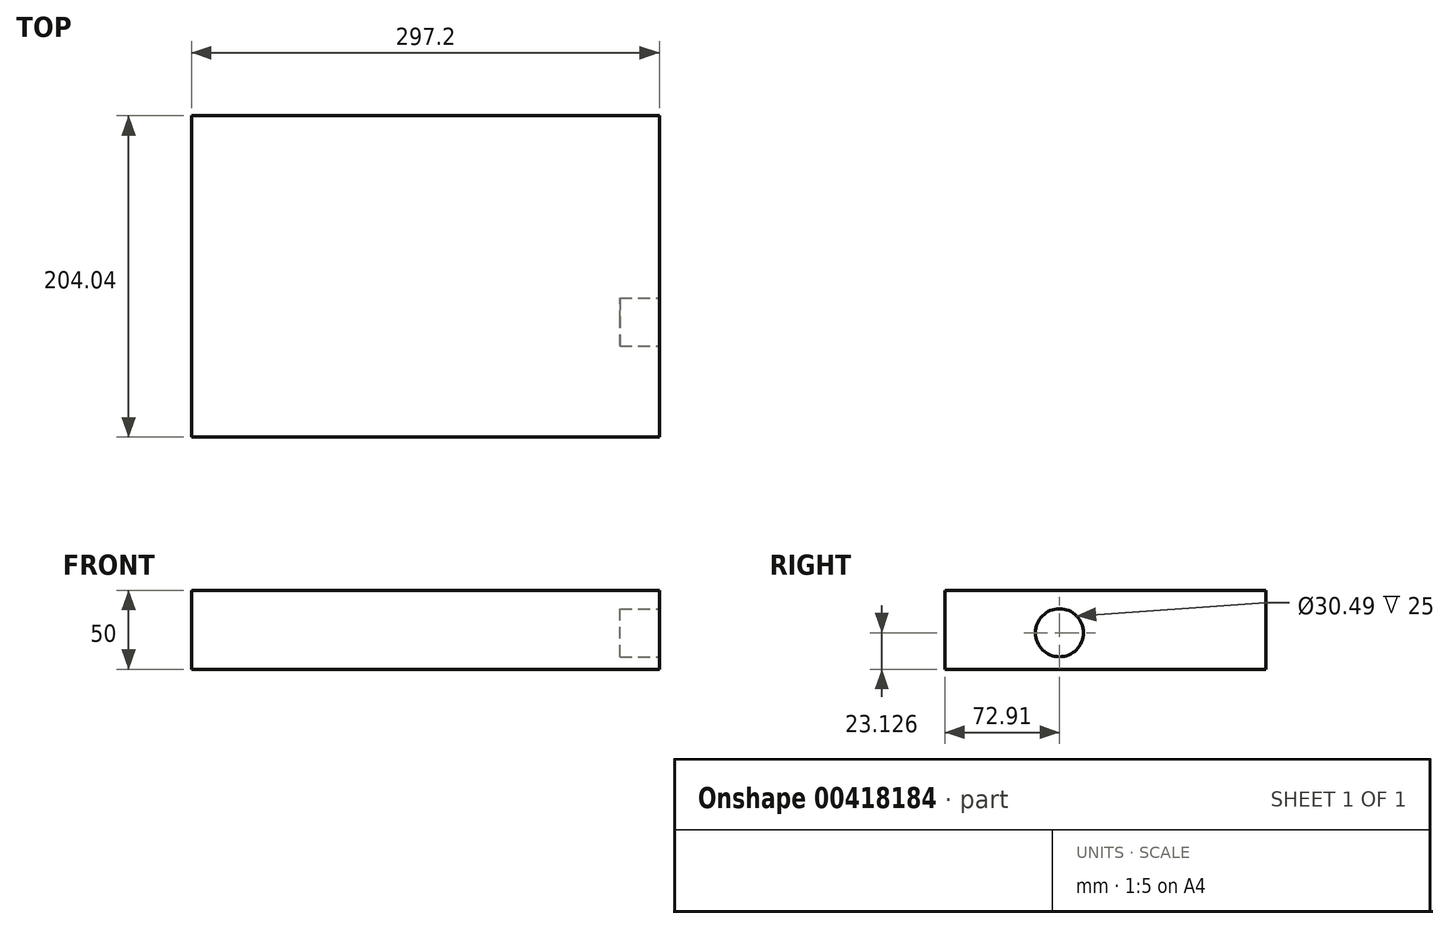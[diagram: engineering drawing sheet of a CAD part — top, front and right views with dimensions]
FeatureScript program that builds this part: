
annotation { "Feature Type Name" : "Feature", "Feature Type Description" : "" }
export const myFeature = defineFeature(function(context is Context, id is Id, definition is map)
    precondition{}
    {
        {
            var Q0;
            Q0=qCreatedBy(makeId("Top.planeOp"),FACE);
            var sketch = newSketch(context, id + "F0", { "sketchPlane" : qUnion([Q0])});
            skLineSegment(sketch, "E0.bottom", {"start": v(89.3, -89.62) * mm, "end": v(-207.89, -89.62) * mm});
            skLineSegment(sketch, "E0.top", {"start": v(89.3, 114.42) * mm, "end": v(-207.89, 114.42) * mm});
            skLineSegment(sketch, "E0.left", {"start": v(89.3, -89.62) * mm, "end": v(89.3, 114.42) * mm});
            skLineSegment(sketch, "E0.right", {"start": v(-207.89, -89.62) * mm, "end": v(-207.89, 114.42) * mm});
            skPoint(sketch, "E0.middle", {"position": v(-59.3, 12.4) * mm});
            skSolve(sketch);
        }
        {
            var Q0;
            Q0 = qSketchRegion(id + "F0", true);
            extrude(context, id + "F1", {"entities" : qUnion([Q0]), "depth" : 50 * mm});
        }
        {
            var Q0;
            Q0=makeQuery(id+"F1.opExtrude","SWEPT_FACE",FACE,{"disambiguationData":[OSD([sQuery(id+"F0.wireOp",EDGE,"E0.left")])]});
            var sketch = newSketch(context, id + "F2", { "sketchPlane" : qUnion([Q0])});
            skCircle(sketch, "E1", {"center": v(-16.7, 23.13) * mm, "radius": 15.24 * mm});
            skSolve(sketch);
        }
        {
            var Q0;
            Q0=makeQuery(id+"F2.imprint","IMPRINT",FACE,{"disambiguationData":[TD([[makeQuery(id+"F2.imprint","IMPRINT",EDGE,{"derivedFrom":sQuery(id+"F2.wireOp",EDGE,"E1")}),1.0]])]});
            var Q1;
            Q1=sQuery(id+"F2.wireOp",EDGE,"E1");
            extrude(context, id + "F3", {"entities" : qUnion([Q0]), "operationType" : NewBodyOperationType.REMOVE, "surfaceEntities" : qUnion([Q1]), "oppositeDirection" : true, "depth" : 25 * mm});
        }
    });
